# Revit family: PRESTO_56602_TOUCH_DECK_MOUNTED_WASHBASIN_SENSITIVE_MIXER_TAP_EN
name_source: partatom
category: Plumbing Fixtures
revit_build: Autodesk Revit 2015 (Build: 20140903_1530(x64)
units: mm (PartAtom-declared; Revit-internal decimal feet)

## types (1)
- Default
    BIMobject category = Taps & Mixers
    BOSUseNativeGeometries = 1
    Cold Water = 0"
    Default Elevation = 4' - 0"
    Design country = France
    Edition number = 1
    Hot Water = 0"
    IFC Classification = Sanitary Terminal
    Manufacturer country = France
    Manufacturer name = Presto
    Material main = Chrome
    Nominal height = 146
    Nominal width = 173
    Presto_BOPCEditionNumber = 1
    Presto_CW_inlet = G'3/8
    Presto_flow = Débit ajustable entre 5 et 26L/min
    Presto_material = laiton
    Presto_operating_pressure = 1 à 5 bar - Pression recommandée : 3 bar
    Presto_outlet = M24X1
    Presto_secondary_material = SPEX
    Presto_warranty = 10
    Product Guid = 50e6745b-ec64-4407-bd04-7f299a9e16d7
    Product SKU = 56602
    Product data url = https://bimobject.com
    Product name = WHITE DECK-MOUNTED MIXER TAP
    QR code = http://bimobject.com
    UNSPSC Code = 301815
    Weight Net (Kg) = 0

## geometry (parser evidence)
native form markers: Sweep x3
no freeform markers — native parametric forms only
